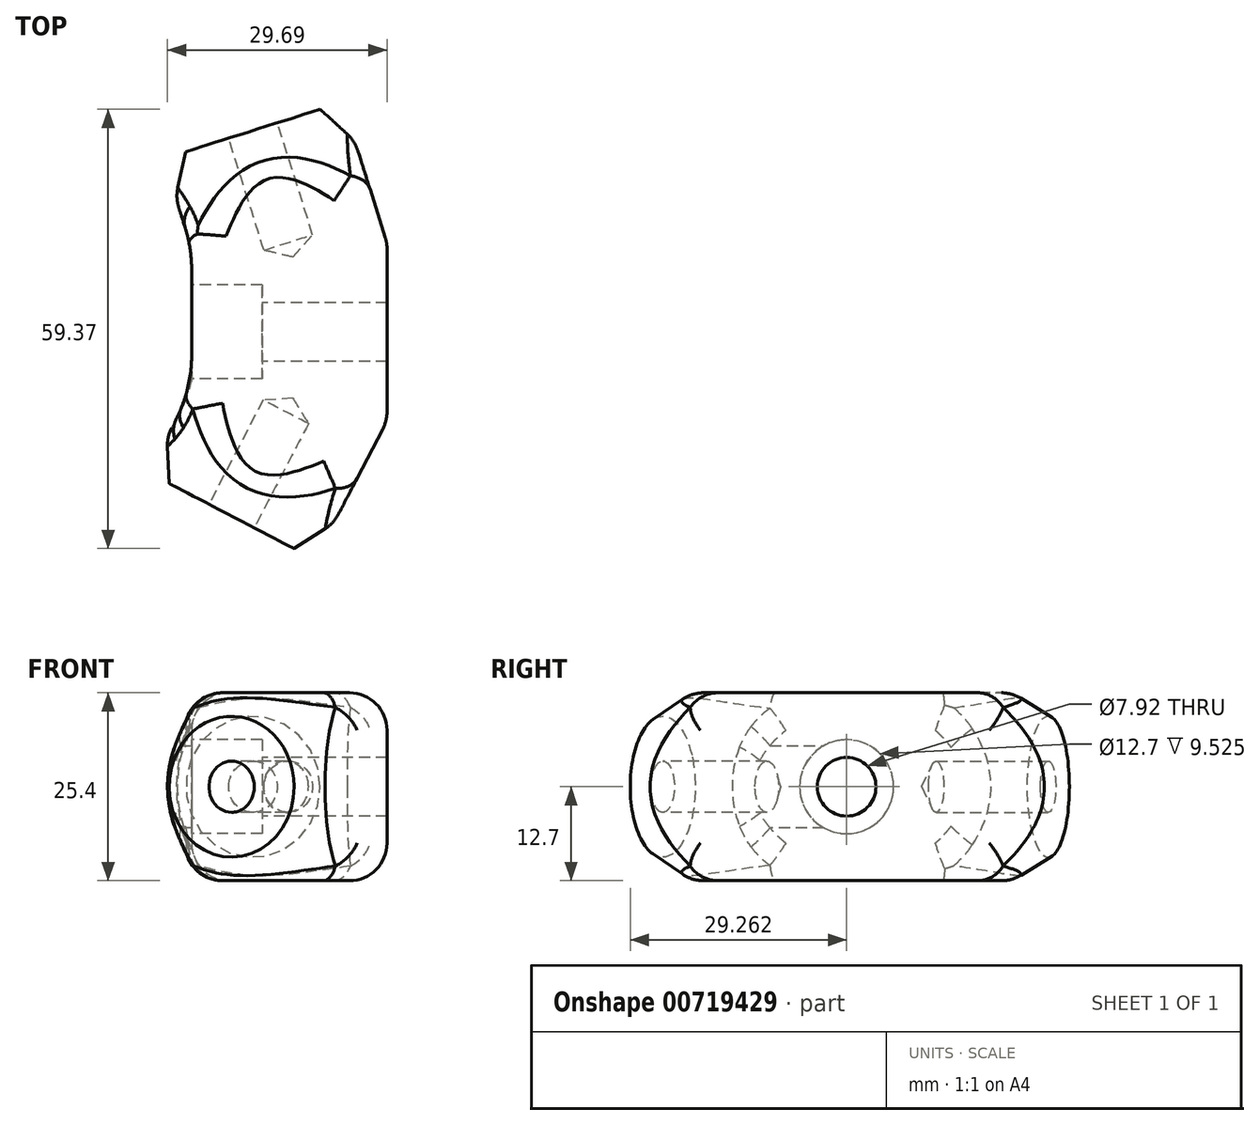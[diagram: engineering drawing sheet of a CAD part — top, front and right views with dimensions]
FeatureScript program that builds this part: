
annotation { "Feature Type Name" : "Feature", "Feature Type Description" : "" }
export const myFeature = defineFeature(function(context is Context, id is Id, definition is map)
    precondition{}
    {
        {
            var Q0;
            Q0=qCreatedBy(makeId("Top.planeOp"),FACE);
            var sketch = newSketch(context, id + "F0", { "sketchPlane" : qUnion([Q0])});
            skLineSegment(sketch, "E0", {"start": v(0, 0) * mm, "end": v(0, 24) * mm});
            skLineSegment(sketch, "E1", {"start": v(0, 24) * mm, "end": v(-6.01, 43.06) * mm});
            skLineSegment(sketch, "E2", {"start": v(-6.01, 43.06) * mm, "end": v(-30.23, 35.43) * mm});
            skLineSegment(sketch, "E3", {"start": v(-30.23, 35.43) * mm, "end": v(-26.42, 23.31) * mm});
            skLineSegment(sketch, "E4", {"start": v(-26.42, 23.31) * mm, "end": v(-26.42, 4.26) * mm});
            skLineSegment(sketch, "E5", {"start": v(-26.42, 4.26) * mm, "end": v(-32.28, -7) * mm});
            skLineSegment(sketch, "E6", {"start": v(-32.28, -7) * mm, "end": v(-9.75, -18.73) * mm});
            skLineSegment(sketch, "E7", {"start": v(-9.75, -18.73) * mm, "end": v(0, 0) * mm});
            skSolve(sketch);
        }
        {
            var Q0;
            Q0 = qSketchRegion(id + "F0", true);
            extrude(context, id + "F1", {"entities" : qUnion([Q0]), "depth" : 25.4 * mm, "offsetDistance" : 25.4 * mm});
        }
        {
            var Q0;
            Q0=makeQuery(id+"F1.opExtrude","SWEPT_FACE",FACE,{"disambiguationData":[OSD([sQuery(id+"F0.wireOp",EDGE,"E4")])]});
            var sketch = newSketch(context, id + "F2", { "sketchPlane" : qUnion([Q0])});
            skLineSegment(sketch, "E8", {"start": v(-12, 0) * mm, "end": v(-12, 25.4) * mm, "construction": true});
            skPoint(sketch, "E9", {"position": v(-12, 12.7) * mm});
            skSolve(sketch);
        }
        {
            var Q0;
            Q0=sQuery(id+"F2.wireOp",VERTEX,"E9");
            var Q1;
            Q1=makeQuery(id+"F1.opExtrude","SWEPT_BODY",BODY,{"disambiguationData":[OSD([sQuery(id+"F0.wireOp",EDGE,"E0"),sQuery(id+"F0.wireOp",EDGE,"E1"),sQuery(id+"F0.wireOp",EDGE,"E2"),sQuery(id+"F0.wireOp",EDGE,"E3"),sQuery(id+"F0.wireOp",EDGE,"E4"),sQuery(id+"F0.wireOp",EDGE,"E5"),sQuery(id+"F0.wireOp",EDGE,"E6"),sQuery(id+"F0.wireOp",EDGE,"E7")])]});
            hole(context, id + "F3", {"style" : HoleStyle.C_BORE, "endStyle" : HoleEndStyle.THROUGH, "holeDiameter" : 7.92 * mm, "cBoreDiameter" : 12.7 * mm, "cBoreDepth" : 9.52 * mm, "majorDiameter" : 6.35 * mm, "isTappedThrough" : true, "tappedDepth" : 12.7 * mm, "tapClearance" : 3, "locations" : qUnion([Q0]), "scope" : qUnion([Q1])});
        }
        {
            var Q0;
            Q0=makeQuery(id+"F1.opExtrude","SWEPT_EDGE",EDGE,{"disambiguationData":[OSD([sQuery(id+"F0.wireOp",EDGE,"E3"),sQuery(id+"F0.wireOp",EDGE,"E4")])]});
            var Q1;
            Q1=makeQuery(id+"F1.opExtrude","SWEPT_EDGE",EDGE,{"disambiguationData":[OSD([sQuery(id+"F0.wireOp",EDGE,"E4"),sQuery(id+"F0.wireOp",EDGE,"E5")])]});
            fillet(context, id + "F4", {"entities" : qUnion([Q0, Q1]), "tangentPropagation" : true, "radius" : 19.05 * mm, "defaultsChanged" : true, "vertexSettings" : [], "allowEdgeOverflow" : false});
        }
        {
            var Q0;
            Q0=makeQuery(id+"F1.opExtrude","SWEPT_FACE",FACE,{"disambiguationData":[OSD([sQuery(id+"F0.wireOp",EDGE,"E6")])]});
            var sketch = newSketch(context, id + "F5", { "sketchPlane" : qUnion([Q0])});
            skPoint(sketch, "E10", {"position": v(-12.7, 12.7) * mm});
            skLineSegment(sketch, "E11", {"start": v(-25.4, 12.7) * mm, "end": v(0, 12.7) * mm, "construction": true});
            skSolve(sketch);
        }
        {
            var Q0;
            Q0=makeQuery(id+"F1.opExtrude","SWEPT_FACE",FACE,{"disambiguationData":[OSD([sQuery(id+"F0.wireOp",EDGE,"E2")])]});
            var sketch = newSketch(context, id + "F6", { "sketchPlane" : qUnion([Q0])});
            skPoint(sketch, "E12", {"position": v(5.48, 12.7) * mm});
            skLineSegment(sketch, "E13", {"start": v(-7.22, 12.7) * mm, "end": v(18.18, 12.7) * mm, "construction": true});
            skSolve(sketch);
        }
        {
            var Q0;
            Q0=makeQuery(id+"F1.opExtrude","CAP_EDGE",EDGE,{"disambiguationData":[OSD([sQuery(id+"F0.wireOp",EDGE,"E2")])],"isStart":true});
            cPoint(context, id + "F7", {"entities" : qUnion([Q0]), "parameter" : 0.5});
        }
        {
            var Q0;
            Q0 = qCreatedBy(id + "F7" ,VERTEX);
            var Q1;
            Q1=makeQuery(id+"F1.opExtrude","SWEPT_FACE",FACE,{"disambiguationData":[OSD([sQuery(id+"F0.wireOp",EDGE,"E1")])]});
            cPlane(context, id + "F8", {"entities" : qUnion([Q0, Q1]), "cplaneType" : CPlaneType.PLANE_POINT, "offset" : 25.4 * mm, "width" : 152.4 * mm, "height" : 152.4 * mm});
        }
        {
            var Q0;
            Q0=qCreatedBy(id+"F8.planeOp",FACE);
            var sketch = newSketch(context, id + "F9", { "sketchPlane" : qUnion([Q0])});
            skLineSegment(sketch, "E14", {"start": v(42.88, 22.23) * mm, "end": v(20.88, 34.93) * mm});
            skLineSegment(sketch, "E15", {"start": v(20.88, 34.93) * mm, "end": v(42.88, 34.93) * mm});
            skLineSegment(sketch, "E16", {"start": v(42.88, 34.93) * mm, "end": v(42.88, 22.23) * mm});
            skPoint(sketch, "E17", {"position": v(42.88, 12.7) * mm});
            skLineSegment(sketch, "E18", {"start": v(42.88, 12.7) * mm, "end": v(37.5, 12.7) * mm, "construction": true});
            skSolve(sketch);
        }
        {
            var Q0;
            Q0 = qSketchRegion(id + "F9", true);
            var Q1;
            Q1=sQuery(id+"F9.wireOp",EDGE,"E18");
            revolve(context, id + "F10", {"operationType" : NewBodyOperationType.REMOVE, "surfaceOperationType" : NewSurfaceOperationType.NEW, "entities" : qUnion([Q0]), "axis" : qUnion([Q1]), "revolveType" : RevolveType.FULL, "oppositeDirection" : true});
        }
        {
            var Q0;
            Q0=makeQuery(id+"F1.opExtrude","CAP_EDGE",EDGE,{"disambiguationData":[OSD([sQuery(id+"F0.wireOp",EDGE,"E6")])],"isStart":true});
            cPoint(context, id + "F11", {"entities" : qUnion([Q0]), "parameter" : 0.5});
        }
        {
            var Q0;
            Q0=makeQuery(id+"F1.opExtrude","SWEPT_FACE",FACE,{"disambiguationData":[OSD([sQuery(id+"F0.wireOp",EDGE,"E5")])]});
            var Q1;
            Q1 = qCreatedBy(id + "F11" ,VERTEX);
            cPlane(context, id + "F12", {"entities" : qUnion([Q0, Q1]), "cplaneType" : CPlaneType.PLANE_POINT, "offset" : 25.4 * mm, "width" : 152.4 * mm, "height" : 152.4 * mm});
        }
        {
            var Q0;
            Q0=qCreatedBy(id+"F12.planeOp",FACE);
            var sketch = newSketch(context, id + "F13", { "sketchPlane" : qUnion([Q0])});
            skLineSegment(sketch, "E19", {"start": v(17.02, 12.7) * mm, "end": v(21.11, 12.7) * mm, "construction": true});
            skLineSegment(sketch, "E20", {"start": v(21.11, 22.23) * mm, "end": v(-0.88, 34.93) * mm});
            skLineSegment(sketch, "E21", {"start": v(-0.88, 34.93) * mm, "end": v(21.11, 34.93) * mm});
            skLineSegment(sketch, "E22", {"start": v(21.11, 34.93) * mm, "end": v(21.11, 22.23) * mm});
            skSolve(sketch);
        }
        {
            var Q0;
            Q0 = qSketchRegion(id + "F13", true);
            var Q1;
            Q1=sQuery(id+"F13.wireOp",EDGE,"E19");
            revolve(context, id + "F14", {"operationType" : NewBodyOperationType.REMOVE, "surfaceOperationType" : NewSurfaceOperationType.NEW, "entities" : qUnion([Q0]), "axis" : qUnion([Q1]), "revolveType" : RevolveType.FULL, "oppositeDirection" : true});
        }
        {
            var Q0;
            Q0=makeQuery(id+"F1.opExtrude","SWEPT_FACE",FACE,{"disambiguationData":[OSD([sQuery(id+"F0.wireOp",EDGE,"E0")])]});
            var sketch = newSketch(context, id + "F15", { "sketchPlane" : qUnion([Q0])});
            skPoint(sketch, "E23", {"position": v(24, 12.7) * mm});
            skSolve(sketch);
        }
        {
            var Q0;
            Q0=sQuery(id+"F6.wireOp",VERTEX,"E12");
            var Q1;
            Q1=makeQuery(id+"F1.opExtrude","SWEPT_BODY",BODY,{"disambiguationData":[OSD([sQuery(id+"F0.wireOp",EDGE,"E0"),sQuery(id+"F0.wireOp",EDGE,"E1"),sQuery(id+"F0.wireOp",EDGE,"E2"),sQuery(id+"F0.wireOp",EDGE,"E3"),sQuery(id+"F0.wireOp",EDGE,"E4"),sQuery(id+"F0.wireOp",EDGE,"E5"),sQuery(id+"F0.wireOp",EDGE,"E6"),sQuery(id+"F0.wireOp",EDGE,"E7")])]});
            hole(context, id + "F16", {"style" : HoleStyle.SIMPLE, "endStyle" : HoleEndStyle.BLIND, "standardTappedOrClearance" : lookupTablePath({ "standard" : "ANSI", "engagement" : "75%", "pitch" : "24 tpi", "size" : "5/16", "type" : "Tapped" }), "standardBlindInLast" : lookupTablePath({ "fit" : "Free", "standard" : "ANSI", "engagement" : "75%", "pitch" : "24 tpi", "size" : "5/16", "type" : "Clearance & tapped" }), "holeDiameter" : 6.9 * mm, "majorDiameter" : 7.94 * mm, "showTappedDepth" : true, "holeDepth" : 15.88 * mm, "isTappedThrough" : true, "tappedDepth" : 12.7 * mm, "tapClearance" : 3, "locations" : qUnion([Q0]), "scope" : qUnion([Q1])});
        }
        {
            var Q0;
            Q0=sQuery(id+"F5.wireOp",VERTEX,"E10");
            var Q1;
            Q1=makeQuery(id+"F1.opExtrude","SWEPT_BODY",BODY,{"disambiguationData":[OSD([sQuery(id+"F0.wireOp",EDGE,"E0"),sQuery(id+"F0.wireOp",EDGE,"E1"),sQuery(id+"F0.wireOp",EDGE,"E2"),sQuery(id+"F0.wireOp",EDGE,"E3"),sQuery(id+"F0.wireOp",EDGE,"E4"),sQuery(id+"F0.wireOp",EDGE,"E5"),sQuery(id+"F0.wireOp",EDGE,"E6"),sQuery(id+"F0.wireOp",EDGE,"E7")])]});
            hole(context, id + "F17", {"style" : HoleStyle.SIMPLE, "endStyle" : HoleEndStyle.BLIND, "standardTappedOrClearance" : lookupTablePath({ "standard" : "ANSI", "engagement" : "75%", "pitch" : "24 tpi", "size" : "5/16", "type" : "Tapped" }), "standardBlindInLast" : lookupTablePath({ "fit" : "Free", "standard" : "ANSI", "engagement" : "75%", "pitch" : "24 tpi", "size" : "5/16", "type" : "Clearance & tapped" }), "holeDiameter" : 6.9 * mm, "majorDiameter" : 7.94 * mm, "showTappedDepth" : true, "holeDepth" : 15.88 * mm, "isTappedThrough" : true, "tappedDepth" : 12.7 * mm, "tapClearance" : 3, "locations" : qUnion([Q0]), "scope" : qUnion([Q1])});
        }
        {
            var Q0;
            Q0=makeQuery(id+"F1.opExtrude","CAP_FACE",FACE,{"disambiguationData":[OSD([sQuery(id+"F0.wireOp",EDGE,"E0"),sQuery(id+"F0.wireOp",EDGE,"E1"),sQuery(id+"F0.wireOp",EDGE,"E2"),sQuery(id+"F0.wireOp",EDGE,"E3"),sQuery(id+"F0.wireOp",EDGE,"E4"),sQuery(id+"F0.wireOp",EDGE,"E5"),sQuery(id+"F0.wireOp",EDGE,"E6"),sQuery(id+"F0.wireOp",EDGE,"E7")])],"isStart":false});
            var Q1;
            Q1=makeQuery(id+"F1.opExtrude","CAP_FACE",FACE,{"disambiguationData":[OSD([sQuery(id+"F0.wireOp",EDGE,"E0"),sQuery(id+"F0.wireOp",EDGE,"E1"),sQuery(id+"F0.wireOp",EDGE,"E2"),sQuery(id+"F0.wireOp",EDGE,"E3"),sQuery(id+"F0.wireOp",EDGE,"E4"),sQuery(id+"F0.wireOp",EDGE,"E5"),sQuery(id+"F0.wireOp",EDGE,"E6"),sQuery(id+"F0.wireOp",EDGE,"E7")])],"isStart":true});
            fillet(context, id + "F18", {"entities" : qUnion([Q0, Q1]), "tangentPropagation" : true, "radius" : 5.08 * mm, "defaultsChanged" : false, "vertexSettings" : [], "allowEdgeOverflow" : false});
        }
        {
            var Q0;
            Q0=makeQuery(id+"F10.boolean.opBoolean","INTERSECT",EDGE,{"derivedFrom":[makeQuery(id+"F1.opExtrude","SWEPT_FACE",FACE,{"disambiguationData":[OSD([sQuery(id+"F0.wireOp",EDGE,"E3")])]}),makeQuery(id+"F10.opRevolve","SWEPT_FACE",FACE,{"disambiguationData":[OSD([sQuery(id+"F9.wireOp",EDGE,"E14")])]})]});
            var Q1;
            Q1=makeQuery(id+"F14.boolean.opBoolean","INTERSECT",EDGE,{"derivedFrom":[makeQuery(id+"F1.opExtrude","SWEPT_FACE",FACE,{"disambiguationData":[OSD([sQuery(id+"F0.wireOp",EDGE,"E5")])]}),makeQuery(id+"F14.opRevolve","SWEPT_FACE",FACE,{"disambiguationData":[OSD([sQuery(id+"F13.wireOp",EDGE,"E20")])]})]});
            var Q2;
            Q2=makeQuery(id+"F1.opExtrude","SWEPT_FACE",FACE,{"disambiguationData":[OSD([sQuery(id+"F0.wireOp",EDGE,"E1")])]});
            var Q3;
            Q3=makeQuery(id+"F1.opExtrude","SWEPT_FACE",FACE,{"disambiguationData":[OSD([sQuery(id+"F0.wireOp",EDGE,"E7")])]});
            fillet(context, id + "F19", {"entities" : qUnion([Q0, Q1, Q2, Q3]), "tangentPropagation" : true, "radius" : 5.08 * mm, "defaultsChanged" : false, "vertexSettings" : [], "allowEdgeOverflow" : false});
        }
    });
